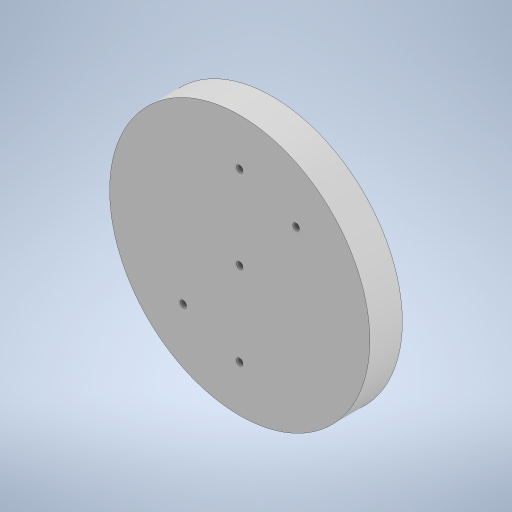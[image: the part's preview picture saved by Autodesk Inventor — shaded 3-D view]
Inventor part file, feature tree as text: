
AUTODESK INVENTOR PART (.ipt)
format: ipt  version: 2023.2 (Build 272271000, 271)  size: 232,448 bytes
history: native  units: mm
features: extrude x2, sketch x2
ambient origin geometry x8: Origin, YZ Plane, XZ Plane, XY Plane, X Axis, Y Axis, Z Axis, Center Point
bodies: Solid1 (feature_tree)
feature tree (4):
  extrude  "Extrusion1"  Depth=1.0mm
  extrude  "Extrusion2"  Depth=5.0mm
  sketch  "Sketch1"  dims[d0=40.0mm d1=1.0mm]
  sketch  "Sketch2"  dims[d2=5.0mm d3=0.0mm d4=12.85mm d5=1.0mm d6=12.85mm d8=1.0mm d9=5.0mm d10=0.0mm d15=90.0deg d17=8.290314mm d18=7.417649mm d20=12.85mm d21=23.125613mm d22=1.0mm d23=12.85mm d24=1.0mm d25=7.417649mm]
